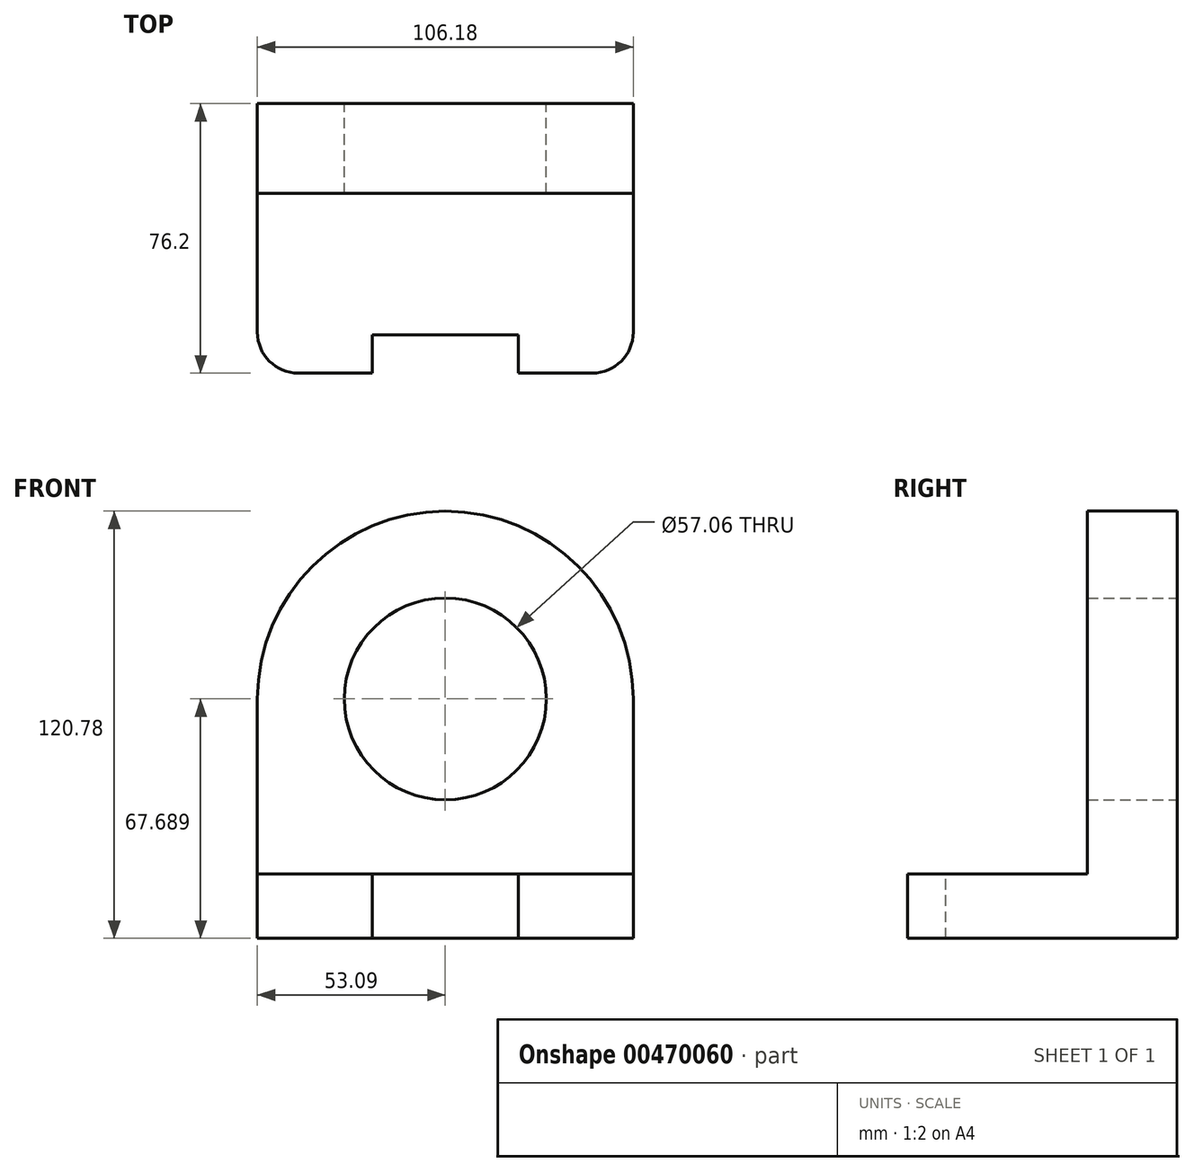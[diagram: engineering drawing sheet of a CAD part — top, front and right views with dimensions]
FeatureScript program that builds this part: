
annotation { "Feature Type Name" : "Feature", "Feature Type Description" : "" }
export const myFeature = defineFeature(function(context is Context, id is Id, definition is map)
    precondition{}
    {
        {
            var Q0;
            Q0=qCreatedBy(makeId("Front.planeOp"),FACE);
            var sketch = newSketch(context, id + "F0", { "sketchPlane" : qUnion([Q0])});
            skLineSegment(sketch, "E0.top", {"start": v(53.09, -62.57) * mm, "end": v(-53.09, -62.57) * mm});
            skLineSegment(sketch, "E0.left", {"start": v(53.09, 5.12) * mm, "end": v(53.09, -62.57) * mm});
            skLineSegment(sketch, "E0.right", {"start": v(-53.09, 5.12) * mm, "end": v(-53.09, -62.57) * mm});
            skPoint(sketch, "E0.middle", {"position": v(0, 0) * mm});
            skLineSegment(sketch, "E1", {"start": v(-53.09, 5.12) * mm, "end": v(53.09, 5.12) * mm, "construction": true});
            skArc(sketch, "E2", {"start": v(53.09, 5.12) * mm, "mid": v(0, 58.2) * mm, "end": v(-53.09, 5.12) * mm});
            skCircle(sketch, "E3", {"center": v(0, 5.12) * mm, "radius": 28.53 * mm});
            skLineSegment(sketch, "E4", {"start": v(-53.09, -44.37) * mm, "end": v(53.09, -44.37) * mm});
            skPoint(sketch, "E0.bottom.end.orphan", {"position": v(-53.09, 62.57) * mm});
            skPoint(sketch, "E5.orphan", {"position": v(53.09, 62.57) * mm});
            skSolve(sketch);
        }
        {
            var Q0;
            {var subQ0=sQuery(id+"F0.wireOp",EDGE,"E2");Q0=makeQuery(id+"F0.imprint","IMPRINT",FACE,{"disambiguationData":[TD([[makeQuery(id+"F0.imprint","IMPRINT",EDGE,{"derivedFrom":subQ0}),1.0]])]});}
            extrude(context, id + "F1", {"entities" : qUnion([Q0]), "depth" : 25.4 * mm});
        }
        {
            var Q0;
            {var subQ0=sQuery(id+"F0.wireOp",EDGE,"E0.top");Q0=makeQuery(id+"F0.imprint","IMPRINT",FACE,{"disambiguationData":[TD([[makeQuery(id+"F0.imprint","IMPRINT",EDGE,{"derivedFrom":subQ0}),-1.0]])]});}
            extrude(context, id + "F2", {"entities" : qUnion([Q0]), "operationType" : NewBodyOperationType.ADD, "depth" : 76.2 * mm});
        }
        {
            var Q0;
            Q0=makeQuery(id+"F2.opExtrude","SWEPT_FACE",FACE,{"disambiguationData":[OSD([sQuery(id+"F0.wireOp",EDGE,"E4")])]});
            var sketch = newSketch(context, id + "F3", { "sketchPlane" : qUnion([Q0])});
            skCircle(sketch, "E6", {"center": v(41.52, -64.63) * mm, "radius": 11.57 * mm});
            skCircle(sketch, "E7", {"center": v(-41.52, -64.63) * mm, "radius": 11.57 * mm});
            skLineSegment(sketch, "E8", {"start": v(0, -76.2) * mm, "end": v(-20.67, -76.2) * mm});
            skLineSegment(sketch, "E9", {"start": v(0, -76.2) * mm, "end": v(20.67, -76.2) * mm});
            skLineSegment(sketch, "E10", {"start": v(-20.67, -76.2) * mm, "end": v(-20.67, -65.41) * mm});
            skLineSegment(sketch, "E11", {"start": v(-20.67, -65.41) * mm, "end": v(20.67, -65.41) * mm});
            skLineSegment(sketch, "E12", {"start": v(20.67, -65.41) * mm, "end": v(20.67, -76.2) * mm});
            skLineSegment(sketch, "E13", {"start": v(-41.52, -76.2) * mm, "end": v(-53.09, -76.2) * mm});
            skLineSegment(sketch, "E14", {"start": v(-53.09, -76.2) * mm, "end": v(-53.09, -64.63) * mm});
            skLineSegment(sketch, "E15", {"start": v(41.52, -76.2) * mm, "end": v(53.09, -76.2) * mm});
            skLineSegment(sketch, "E16", {"start": v(53.09, -76.2) * mm, "end": v(53.09, -64.63) * mm});
            skLineSegment(sketch, "E17", {"start": v(20.67, -76.2) * mm, "end": v(-20.67, -76.2) * mm});
            skSolve(sketch);
        }
        {
            var Q0;
            {var subQ0=sQuery(id+"F3.wireOp",EDGE,"E15");Q0=makeQuery(id+"F3.imprint","IMPRINT",FACE,{"disambiguationData":[TD([[makeQuery(id+"F3.imprint","IMPRINT",EDGE,{"derivedFrom":subQ0}),1.0]])]});}
            var Q1;
            {var subQ0=sQuery(id+"F3.wireOp",EDGE,"E13");Q1=makeQuery(id+"F3.imprint","IMPRINT",FACE,{"disambiguationData":[TD([[makeQuery(id+"F3.imprint","IMPRINT",EDGE,{"derivedFrom":subQ0}),1.0]])]});}
            var Q2;
            Q2=makeQuery(id+"F3.imprint","IMPRINT",FACE,{"disambiguationData":[TD([[makeQuery(id+"F3.imprint","IMPRINT",EDGE,{"derivedFrom":sQuery(id+"F3.wireOp",EDGE,"E10")}),-1.0]])]});
            extrude(context, id + "F4", {"entities" : qUnion([Q0, Q1, Q2]), "operationType" : NewBodyOperationType.REMOVE, "endBound" : BoundingType.THROUGH_ALL, "oppositeDirection" : true, "depth" : 25.4 * mm});
        }
    });
